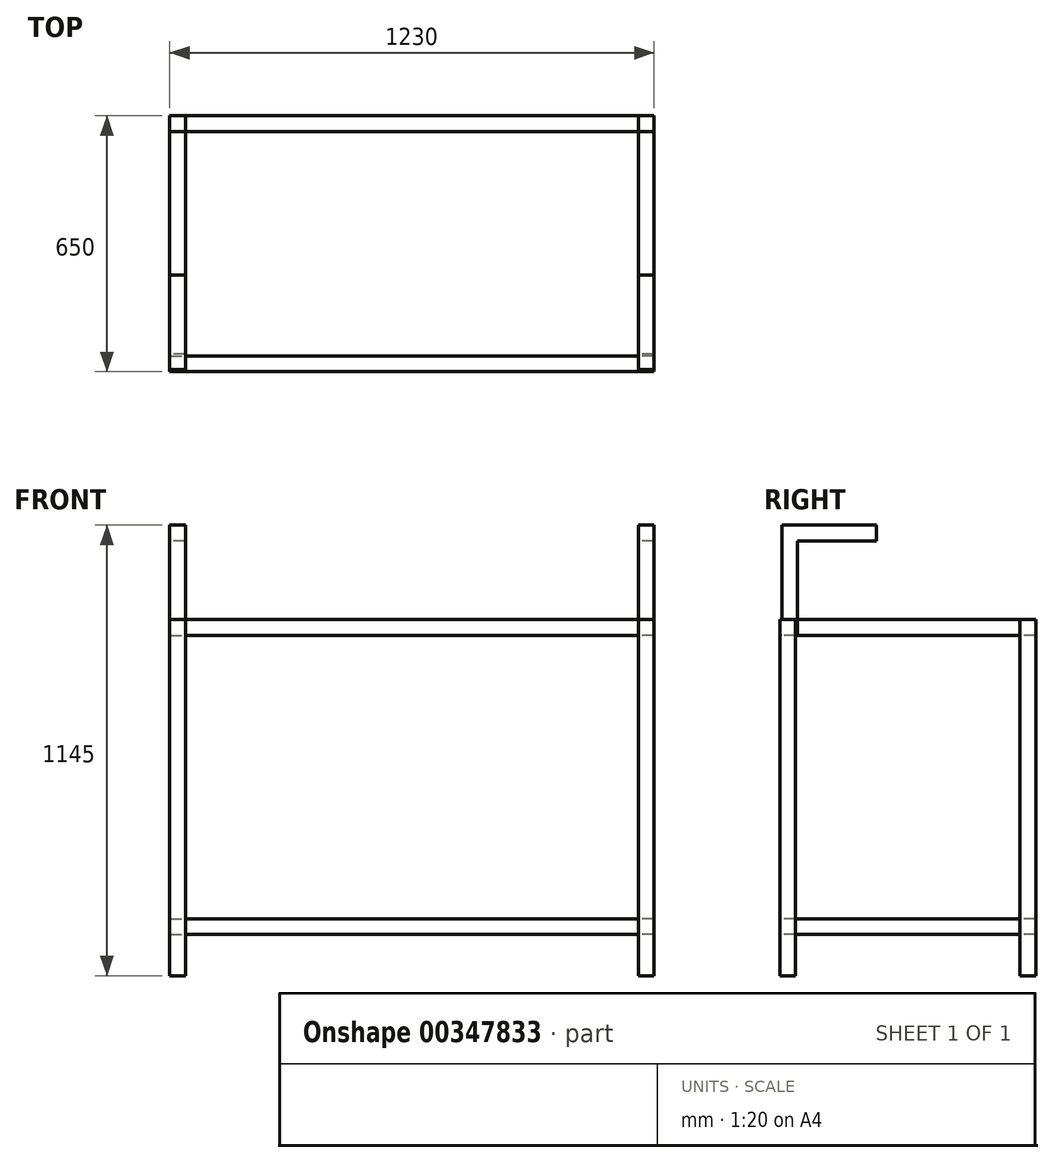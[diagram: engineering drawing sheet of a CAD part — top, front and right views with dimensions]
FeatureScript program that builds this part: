
annotation { "Feature Type Name" : "Feature", "Feature Type Description" : "" }
export const myFeature = defineFeature(function(context is Context, id is Id, definition is map)
    precondition{}
    {
        {
            var Q0;
            Q0=qCreatedBy(makeId("Top.planeOp"),FACE);
            var sketch = newSketch(context, id + "F0", { "sketchPlane" : qUnion([Q0])});
            skLineSegment(sketch, "E0.bottom", {"start": v(615, -325) * mm, "end": v(-615, -325) * mm});
            skLineSegment(sketch, "E0.top", {"start": v(615, 325) * mm, "end": v(-615, 325) * mm});
            skLineSegment(sketch, "E0.left", {"start": v(615, -325) * mm, "end": v(615, 325) * mm});
            skLineSegment(sketch, "E0.right", {"start": v(-615, -325) * mm, "end": v(-615, 325) * mm});
            skPoint(sketch, "E0.middle", {"position": v(0, 0) * mm});
            skLineSegment(sketch, "E1", {"start": v(-575, 325) * mm, "end": v(-575, -325) * mm});
            skLineSegment(sketch, "E2", {"start": v(-615, 285) * mm, "end": v(-575, 285) * mm});
            skLineSegment(sketch, "E3.MirrorCS", {"start": v(575, 325) * mm, "end": v(575, -325) * mm});
            skLineSegment(sketch, "E4.MirrorCS", {"start": v(-615, -285) * mm, "end": v(-575, -285) * mm});
            skLineSegment(sketch, "E5.MirrorCS", {"start": v(615, 285) * mm, "end": v(575, 285) * mm});
            skLineSegment(sketch, "E6.MirrorCS", {"start": v(615, -285) * mm, "end": v(575, -285) * mm});
            skLineSegment(sketch, "E7", {"start": v(-575, 285) * mm, "end": v(575, 285) * mm});
            skLineSegment(sketch, "E8", {"start": v(-575, -285) * mm, "end": v(575, -285) * mm});
            skSolve(sketch);
        }
        {
            var Q0;
            {var subQ5=sQuery(id+"F0.wireOp",EDGE,"E5.MirrorCS");Q0=makeQuery(id+"F0.imprint","IMPRINT",FACE,{"disambiguationData":[TD([[makeQuery(id+"F0.imprint","IMPRINT",EDGE,{"derivedFrom":subQ5}),-1.0]])]});}
            var Q1;
            {var subQ5=sQuery(id+"F0.wireOp",EDGE,"E2");Q1=makeQuery(id+"F0.imprint","IMPRINT",FACE,{"disambiguationData":[TD([[makeQuery(id+"F0.imprint","IMPRINT",EDGE,{"derivedFrom":subQ5}),1.0]])]});}
            var Q2;
            {var subQ5=sQuery(id+"F0.wireOp",EDGE,"E4.MirrorCS");Q2=makeQuery(id+"F0.imprint","IMPRINT",FACE,{"disambiguationData":[TD([[makeQuery(id+"F0.imprint","IMPRINT",EDGE,{"derivedFrom":subQ5}),-1.0]])]});}
            var Q3;
            {var subQ5=sQuery(id+"F0.wireOp",EDGE,"E6.MirrorCS");Q3=makeQuery(id+"F0.imprint","IMPRINT",FACE,{"disambiguationData":[TD([[makeQuery(id+"F0.imprint","IMPRINT",EDGE,{"derivedFrom":subQ5}),1.0]])]});}
            extrude(context, id + "F1", {"entities" : qUnion([Q0, Q1, Q2, Q3]), "depth" : 760 * mm, "hasSecondDirection" : true, "secondDirectionOppositeDirection" : true, "secondDirectionDepth" : 145 * mm});
        }
        {
            var Q0;
            Q0=makeQuery(id+"F1.opExtrude","CAP_FACE",FACE,{"disambiguationData":[OSD([sQuery(id+"F0.wireOp",EDGE,"E0.bottom"),sQuery(id+"F0.wireOp",EDGE,"E0.left"),sQuery(id+"F0.wireOp",EDGE,"E3.MirrorCS"),sQuery(id+"F0.wireOp",EDGE,"E6.MirrorCS")])],"isStart":false});
            var sketch = newSketch(context, id + "F2", { "sketchPlane" : qUnion([Q0])});
            skLineSegment(sketch, "E9.bottom", {"start": v(615, -325) * mm, "end": v(-615, -325) * mm});
            skLineSegment(sketch, "E9.top", {"start": v(615, 325) * mm, "end": v(-615, 325) * mm});
            skLineSegment(sketch, "E9.left", {"start": v(615, -325) * mm, "end": v(615, 325) * mm});
            skLineSegment(sketch, "E9.right", {"start": v(-615, -325) * mm, "end": v(-615, 325) * mm});
            skPoint(sketch, "E9.middle", {"position": v(0, 0) * mm});
            skLineSegment(sketch, "E10", {"start": v(-575, 325) * mm, "end": v(-575, -325) * mm});
            skLineSegment(sketch, "E11", {"start": v(-615, 285) * mm, "end": v(-575, 285) * mm});
            skLineSegment(sketch, "E12.MirrorCS", {"start": v(575, 325) * mm, "end": v(575, -325) * mm});
            skLineSegment(sketch, "E13.MirrorCS", {"start": v(-615, -285) * mm, "end": v(-575, -285) * mm});
            skLineSegment(sketch, "E14.MirrorCS", {"start": v(615, 285) * mm, "end": v(575, 285) * mm});
            skLineSegment(sketch, "E15.MirrorCS", {"start": v(615, -285) * mm, "end": v(575, -285) * mm});
            skLineSegment(sketch, "E16", {"start": v(-575, 285) * mm, "end": v(575, 285) * mm});
            skLineSegment(sketch, "E17", {"start": v(-575, -285) * mm, "end": v(575, -285) * mm});
            skLineSegment(sketch, "E18.bottom", {"start": v(-615, -320) * mm, "end": v(-575, -320) * mm});
            skLineSegment(sketch, "E18.top", {"start": v(-615, -280) * mm, "end": v(-575, -280) * mm});
            skLineSegment(sketch, "E18.left", {"start": v(-615, -320) * mm, "end": v(-615, -280) * mm});
            skLineSegment(sketch, "E18.right", {"start": v(-575, -320) * mm, "end": v(-575, -280) * mm});
            skLineSegment(sketch, "E19.MirrorCS", {"start": v(615, -320) * mm, "end": v(575, -320) * mm});
            skLineSegment(sketch, "E20.MirrorCS", {"start": v(615, -280) * mm, "end": v(575, -280) * mm});
            skSolve(sketch);
        }
        {
            var Q0;
            {var subQ5=sQuery(id+"F2.wireOp",EDGE,"E16");Q0=makeQuery(id+"F2.imprint","IMPRINT",FACE,{"disambiguationData":[TD([[makeQuery(id+"F2.imprint","IMPRINT",EDGE,{"derivedFrom":subQ5}),1.0]])]});}
            var Q1;
            {var subQ2=sQuery(id+"F2.wireOp",EDGE,"E14.MirrorCS");Q1=makeQuery(id+"F2.imprint","IMPRINT",FACE,{"disambiguationData":[TD([[makeQuery(id+"F2.imprint","IMPRINT",EDGE,{"derivedFrom":subQ2}),1.0]])]});}
            var Q2;
            {var subQ5=sQuery(id+"F2.wireOp",EDGE,"E17");Q2=makeQuery(id+"F2.imprint","IMPRINT",FACE,{"disambiguationData":[TD([[makeQuery(id+"F2.imprint","IMPRINT",EDGE,{"derivedFrom":subQ5}),-1.0]])]});}
            var Q3;
            {var subQ0=sQuery(id+"F2.wireOp",EDGE,"E11");Q3=makeQuery(id+"F2.imprint","IMPRINT",FACE,{"disambiguationData":[TD([[makeQuery(id+"F2.imprint","IMPRINT",EDGE,{"derivedFrom":subQ0}),-1.0]])]});}
            var Q4;
            {var subQ0=sQuery(id+"F2.wireOp",EDGE,"E13.MirrorCS");Q4=makeQuery(id+"F2.imprint","IMPRINT",FACE,{"disambiguationData":[TD([[makeQuery(id+"F2.imprint","IMPRINT",EDGE,{"derivedFrom":subQ0}),1.0]])]});}
            var Q5;
            {var subQ0=sQuery(id+"F2.wireOp",EDGE,"E15.MirrorCS");Q5=makeQuery(id+"F2.imprint","IMPRINT",FACE,{"disambiguationData":[TD([[makeQuery(id+"F2.imprint","IMPRINT",EDGE,{"derivedFrom":subQ0}),-1.0]])]});}
            extrude(context, id + "F3", {"entities" : qUnion([Q0, Q1, Q2, Q3, Q4, Q5]), "oppositeDirection" : true, "depth" : 40 * mm});
        }
        {
            var Q0;
            {var subQ5=sQuery(id+"F0.wireOp",EDGE,"E8");Q0=makeQuery(id+"F0.imprint","IMPRINT",FACE,{"disambiguationData":[TD([[makeQuery(id+"F0.imprint","IMPRINT",EDGE,{"derivedFrom":subQ5}),-1.0]])]});}
            var Q1;
            {var subQ0=sQuery(id+"F0.wireOp",EDGE,"E5.MirrorCS");Q1=makeQuery(id+"F0.imprint","IMPRINT",FACE,{"disambiguationData":[TD([[makeQuery(id+"F0.imprint","IMPRINT",EDGE,{"derivedFrom":subQ0}),1.0]])]});}
            var Q2;
            {var subQ5=sQuery(id+"F0.wireOp",EDGE,"E7");Q2=makeQuery(id+"F0.imprint","IMPRINT",FACE,{"disambiguationData":[TD([[makeQuery(id+"F0.imprint","IMPRINT",EDGE,{"derivedFrom":subQ5}),1.0]])]});}
            var Q3;
            {var subQ0=sQuery(id+"F0.wireOp",EDGE,"E2");Q3=makeQuery(id+"F0.imprint","IMPRINT",FACE,{"disambiguationData":[TD([[makeQuery(id+"F0.imprint","IMPRINT",EDGE,{"derivedFrom":subQ0}),-1.0]])]});}
            extrude(context, id + "F4", {"entities" : qUnion([Q0, Q1, Q2, Q3]), "oppositeDirection" : true, "depth" : 40 * mm});
        }
        {
            var Q0;
            {var subQ0=sQuery(id+"F2.wireOp",EDGE,"E13.MirrorCS");Q0=makeQuery(id+"F2.imprint","IMPRINT",FACE,{"disambiguationData":[TD([[makeQuery(id+"F2.imprint","IMPRINT",EDGE,{"derivedFrom":subQ0}),-1.0]])]});}
            var Q1;
            {var subQ0=sQuery(id+"F2.wireOp",EDGE,"E13.MirrorCS");Q1=makeQuery(id+"F2.imprint","IMPRINT",FACE,{"disambiguationData":[TD([[makeQuery(id+"F2.imprint","IMPRINT",EDGE,{"derivedFrom":subQ0}),1.0]])]});}
            var Q2;
            {var subQ0=sQuery(id+"F2.wireOp",EDGE,"E15.MirrorCS");Q2=makeQuery(id+"F2.imprint","IMPRINT",FACE,{"disambiguationData":[TD([[makeQuery(id+"F2.imprint","IMPRINT",EDGE,{"derivedFrom":subQ0}),1.0]])]});}
            var Q3;
            {var subQ0=sQuery(id+"F2.wireOp",EDGE,"E15.MirrorCS");Q3=makeQuery(id+"F2.imprint","IMPRINT",FACE,{"disambiguationData":[TD([[makeQuery(id+"F2.imprint","IMPRINT",EDGE,{"derivedFrom":subQ0}),-1.0]])]});}
            extrude(context, id + "F5", {"entities" : qUnion([Q0, Q1, Q2, Q3]), "depth" : 240 * mm});
        }
        {
            var Q0;
            Q0=makeQuery(id+"F5.opExtrude","SWEPT_FACE",FACE,{"disambiguationData":[OSD([sQuery(id+"F2.wireOp",EDGE,"E20.MirrorCS")])]});
            var sketch = newSketch(context, id + "F6", { "sketchPlane" : qUnion([Q0])});
            skLineSegment(sketch, "E21.bottom", {"start": v(-615, 1000) * mm, "end": v(-575, 1000) * mm});
            skLineSegment(sketch, "E21.top", {"start": v(-615, 960) * mm, "end": v(-575, 960) * mm});
            skLineSegment(sketch, "E21.left", {"start": v(-615, 1000) * mm, "end": v(-615, 960) * mm});
            skLineSegment(sketch, "E21.right", {"start": v(-575, 1000) * mm, "end": v(-575, 960) * mm});
            skSolve(sketch);
        }
        {
            var Q0;
            Q0=makeQuery(id+"F6.imprint","IMPRINT",FACE,{"disambiguationData":[TD([[makeQuery(id+"F6.imprint","IMPRINT",EDGE,{"derivedFrom":sQuery(id+"F6.wireOp",EDGE,"E21.bottom")}),-1.0]])]});
            extrude(context, id + "F7", {"entities" : qUnion([Q0]), "operationType" : NewBodyOperationType.ADD, "depth" : 200 * mm});
        }
        {
            var Q0;
            Q0=makeQuery(id+"F5.opExtrude","SWEPT_FACE",FACE,{"disambiguationData":[OSD([sQuery(id+"F2.wireOp",EDGE,"E18.top")])]});
            var sketch = newSketch(context, id + "F8", { "sketchPlane" : qUnion([Q0])});
            skLineSegment(sketch, "E22.bottom", {"start": v(575, 1000) * mm, "end": v(615, 1000) * mm});
            skLineSegment(sketch, "E22.top", {"start": v(575, 960) * mm, "end": v(615, 960) * mm});
            skLineSegment(sketch, "E22.left", {"start": v(575, 1000) * mm, "end": v(575, 960) * mm});
            skLineSegment(sketch, "E22.right", {"start": v(615, 1000) * mm, "end": v(615, 960) * mm});
            skSolve(sketch);
        }
        {
            var Q0;
            Q0=makeQuery(id+"F8.imprint","IMPRINT",FACE,{"disambiguationData":[TD([[makeQuery(id+"F8.imprint","IMPRINT",EDGE,{"derivedFrom":sQuery(id+"F8.wireOp",EDGE,"E22.bottom")}),1.0]])]});
            extrude(context, id + "F9", {"entities" : qUnion([Q0]), "operationType" : NewBodyOperationType.ADD, "depth" : 200 * mm});
        }
    });
